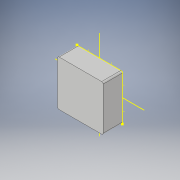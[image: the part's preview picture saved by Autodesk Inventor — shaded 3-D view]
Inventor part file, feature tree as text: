
AUTODESK INVENTOR PART (.ipt)
format: ipt  version: 2019 (Build 230136000, 136)  size: 120,320 bytes
history: native  units: in
note: dims shown in document units (in); Inventor stores cm internally (conversion verified against a paired STEP export)
features: other x3, sketch x2, extrude x1
ambient origin geometry x8: Origin, YZ Plane, XZ Plane, XY Plane, X Axis, Y Axis, Z Axis, Center Point
bodies: Solid1 (feature_tree)
feature tree (6):
  other  "Front Ring"
  extrude  "Extrusion2"  Depth=1.0in TaperAngle=0.0deg
  other  "Solid2::Front Ring"
  other  "TaggingFeature1"
  sketch  "Sketch3"
  sketch  "Sketch2"  dims[d0=0.3937in d3=1.0in d4=0.0in]
